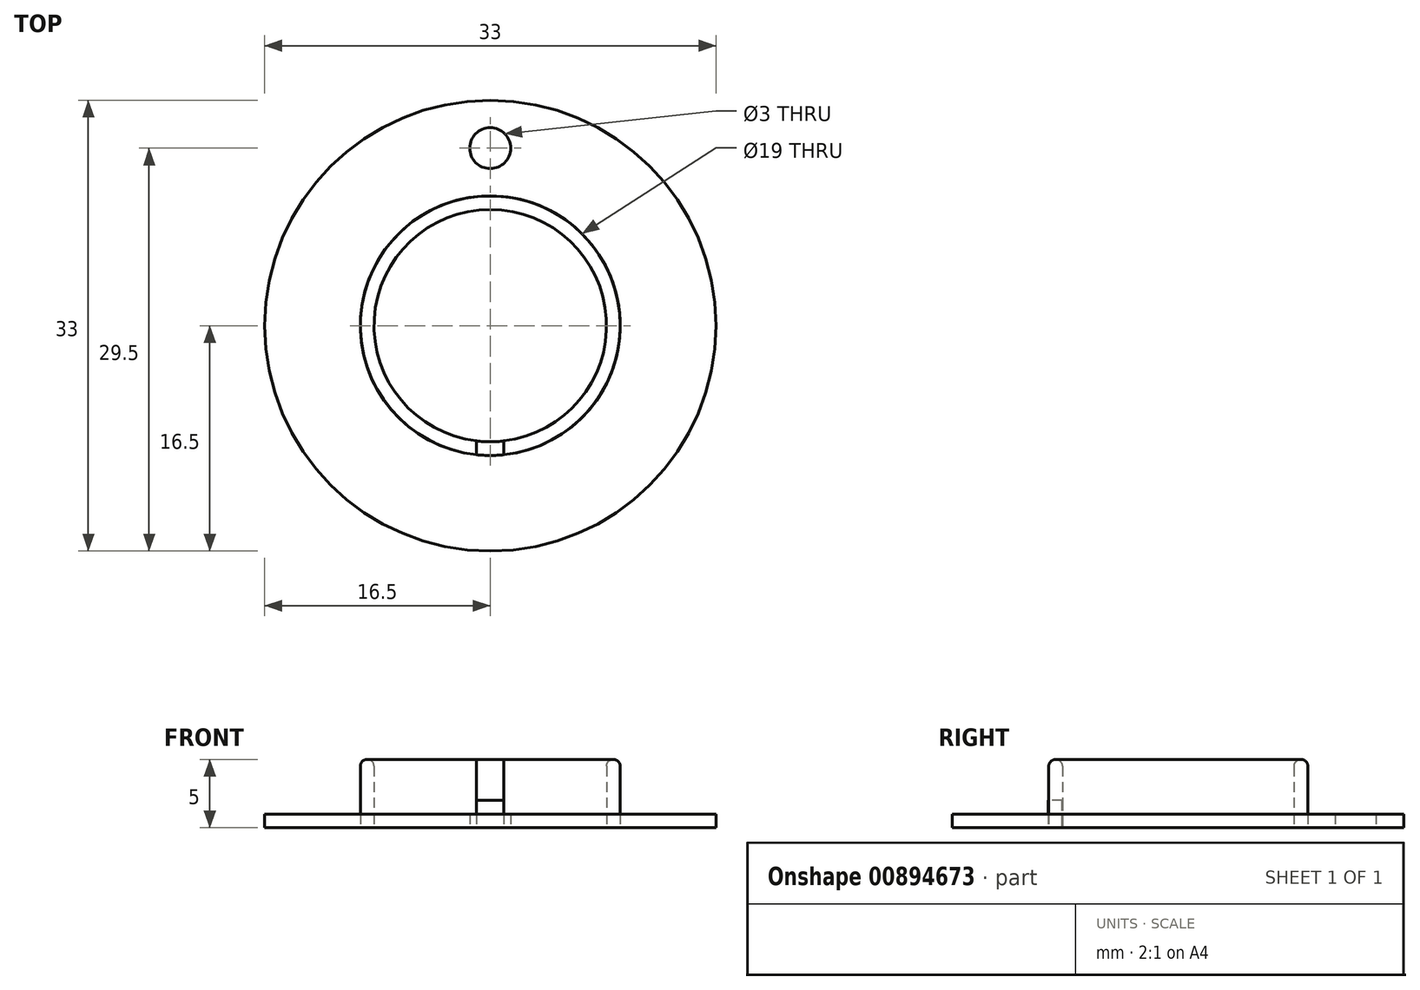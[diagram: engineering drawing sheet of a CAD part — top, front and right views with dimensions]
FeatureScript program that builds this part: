
annotation { "Feature Type Name" : "Feature", "Feature Type Description" : "" }
export const myFeature = defineFeature(function(context is Context, id is Id, definition is map)
    precondition{}
    {
        {
            var Q0;
            Q0=qCreatedBy(makeId("Top.planeOp"),FACE);
            var sketch = newSketch(context, id + "F0", { "sketchPlane" : qUnion([Q0])});
            skCircle(sketch, "E0", {"center": v(0, 0) * mm, "radius": 16.5 * mm});
            skCircle(sketch, "E1", {"center": v(0, 13) * mm, "radius": 1.5 * mm});
            skCircle(sketch, "E2", {"center": v(0, 0) * mm, "radius": 9.5 * mm});
            skCircle(sketch, "E3", {"center": v(0, 0) * mm, "radius": 8.5 * mm});
            skLineSegment(sketch, "E4", {"start": v(-1, -7.92) * mm, "end": v(-1, -10.26) * mm});
            skLineSegment(sketch, "E5", {"start": v(1, -7.84) * mm, "end": v(1, -10.31) * mm});
            skSolve(sketch);
        }
        {
            var Q0;
            Q0=makeQuery(id+"F0.imprint","IMPRINT",FACE,{"disambiguationData":[TD([[makeQuery(id+"F0.imprint","IMPRINT",EDGE,{"derivedFrom":sQuery(id+"F0.wireOp",EDGE,"E0")}),1.0]])]});
            var Q1;
            {var subQ0=sQuery(id+"F0.wireOp",EDGE,"E3");var subQ1=makeQuery(id+"F0.imprint","INTERSECT",VERTEX,{"derivedFrom":[subQ0,sQuery(id+"F0.wireOp",EDGE,"E4")]});Q1=makeQuery(id+"F0.imprint","IMPRINT",FACE,{"disambiguationData":[TD([[makeQuery(id+"F0.imprint","IMPRINT",EDGE,{"disambiguationData":[TD([[subQ1,-1.0]])],"derivedFrom":subQ0}),1.0]])]});}
            extrude(context, id + "F1", {"entities" : qUnion([Q0, Q1]), "depth" : 1 * mm, "offsetDistance" : 25 * mm});
        }
        {
            var Q0;
            {var subQ0=sQuery(id+"F0.wireOp",EDGE,"E4");var subQ1=sQuery(id+"F0.wireOp",EDGE,"E2");var subQ2=makeQuery(id+"F0.imprint","INTERSECT",VERTEX,{"derivedFrom":[subQ1,subQ0]});Q0=makeQuery(id+"F0.imprint","IMPRINT",FACE,{"disambiguationData":[TD([[makeQuery(id+"F0.imprint","IMPRINT",EDGE,{"disambiguationData":[TD([[subQ2,1.0]])],"derivedFrom":subQ1}),1.0]])]});}
            extrude(context, id + "F2", {"entities" : qUnion([Q0]), "depth" : 5 * mm, "offsetDistance" : 25 * mm});
        }
        {
            var Q0;
            {var subQ0=sQuery(id+"F0.wireOp",EDGE,"E4");var subQ1=sQuery(id+"F0.wireOp",EDGE,"E2");var subQ2=makeQuery(id+"F0.imprint","INTERSECT",VERTEX,{"derivedFrom":[subQ1,subQ0]});Q0=makeQuery(id+"F0.imprint","IMPRINT",FACE,{"disambiguationData":[TD([[makeQuery(id+"F0.imprint","IMPRINT",EDGE,{"disambiguationData":[TD([[subQ2,-1.0]])],"derivedFrom":subQ1}),1.0]])]});}
            extrude(context, id + "F3", {"entities" : qUnion([Q0]), "depth" : 2 * mm, "offsetDistance" : 25 * mm});
        }
        {
            var Q0;
            Q0=makeQuery(id+"F2.opExtrude","CAP_EDGE",EDGE,{"disambiguationData":[OSD([sQuery(id+"F0.wireOp",EDGE,"E2")])],"isStart":false});
            var Q1;
            Q1=makeQuery(id+"F2.opExtrude","CAP_EDGE",EDGE,{"disambiguationData":[OSD([sQuery(id+"F0.wireOp",EDGE,"E3")])],"isStart":false});
            fillet(context, id + "F4", {"entities" : qUnion([Q0, Q1]), "radius" : 0.5 * mm, "tangentPropagation" : true, "allowEdgeOverflow" : false});
        }
    });
